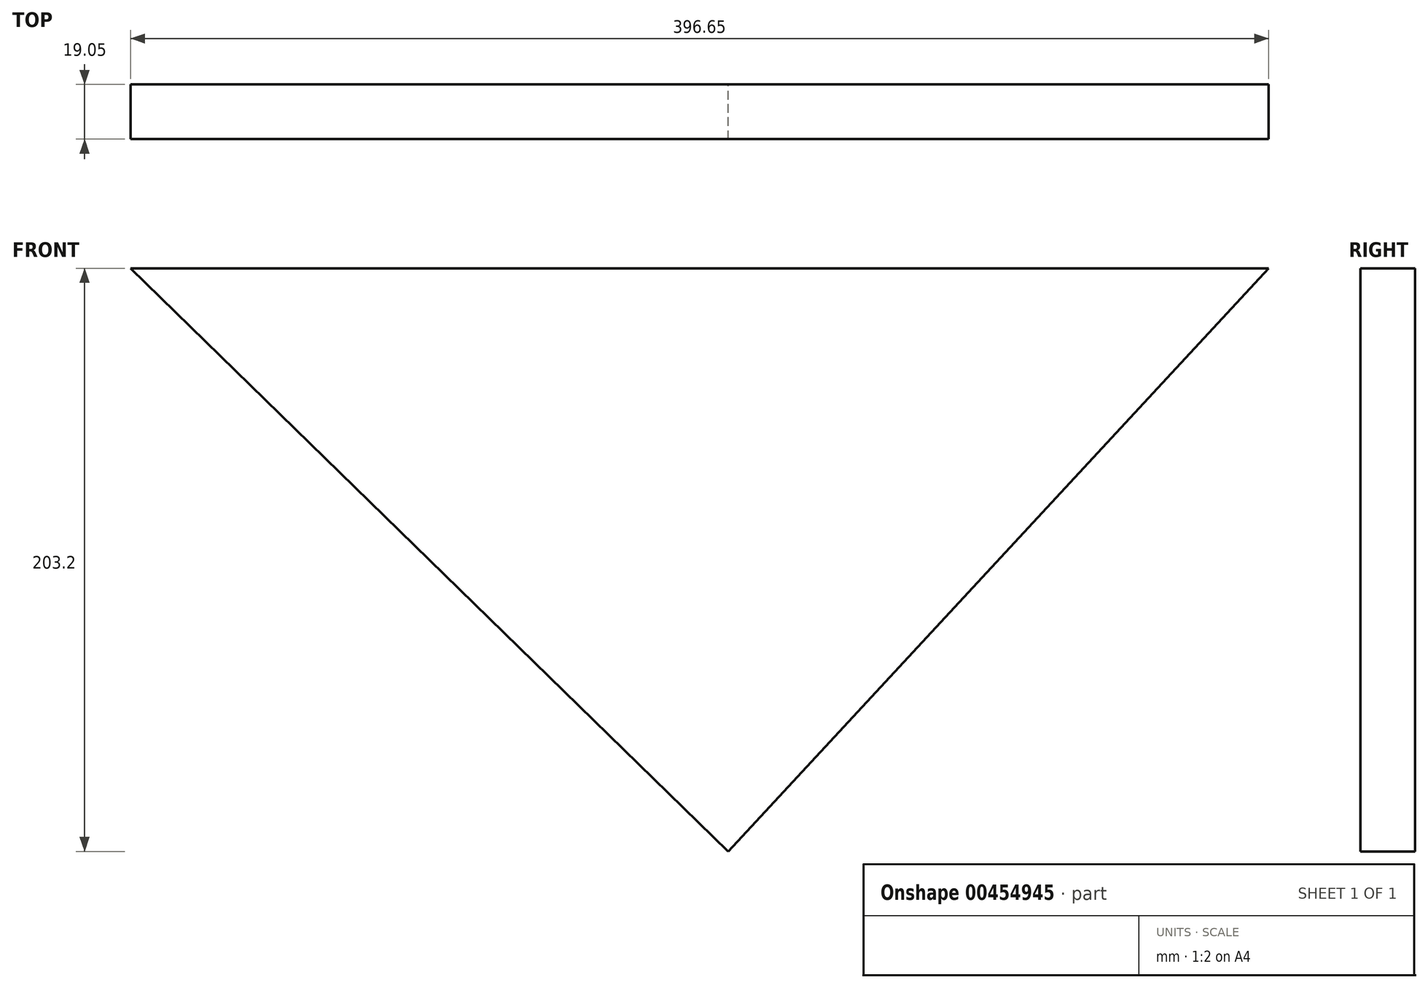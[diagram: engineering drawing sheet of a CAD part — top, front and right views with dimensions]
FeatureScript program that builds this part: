
annotation { "Feature Type Name" : "Feature", "Feature Type Description" : "" }
export const myFeature = defineFeature(function(context is Context, id is Id, definition is map)
    precondition{}
    {
        {
            var Q0;
            Q0=qCreatedBy(makeId("Front.planeOp"),FACE);
            var sketch = newSketch(context, id + "F0", { "sketchPlane" : qUnion([Q0])});
            skLineSegment(sketch, "E0", {"start": v(-208.33, 76.68) * mm, "end": v(198.07, 76.68) * mm});
            skLineSegment(sketch, "E1", {"start": v(-208.33, 76.68) * mm, "end": v(0, -126.52) * mm});
            skLineSegment(sketch, "E2", {"start": v(-5.13, 76.68) * mm, "end": v(0, -126.52) * mm});
            skLineSegment(sketch, "E3.MirrorCS", {"start": v(197.81, 86.93) * mm, "end": v(0, -126.52) * mm});
            skSolve(sketch);
        }
        {
            var Q0;
            Q0 = qSketchRegion(id + "F0", true);
            extrude(context, id + "F1", {"entities" : qUnion([Q0]), "depth" : 19.05 * mm});
        }
    });
